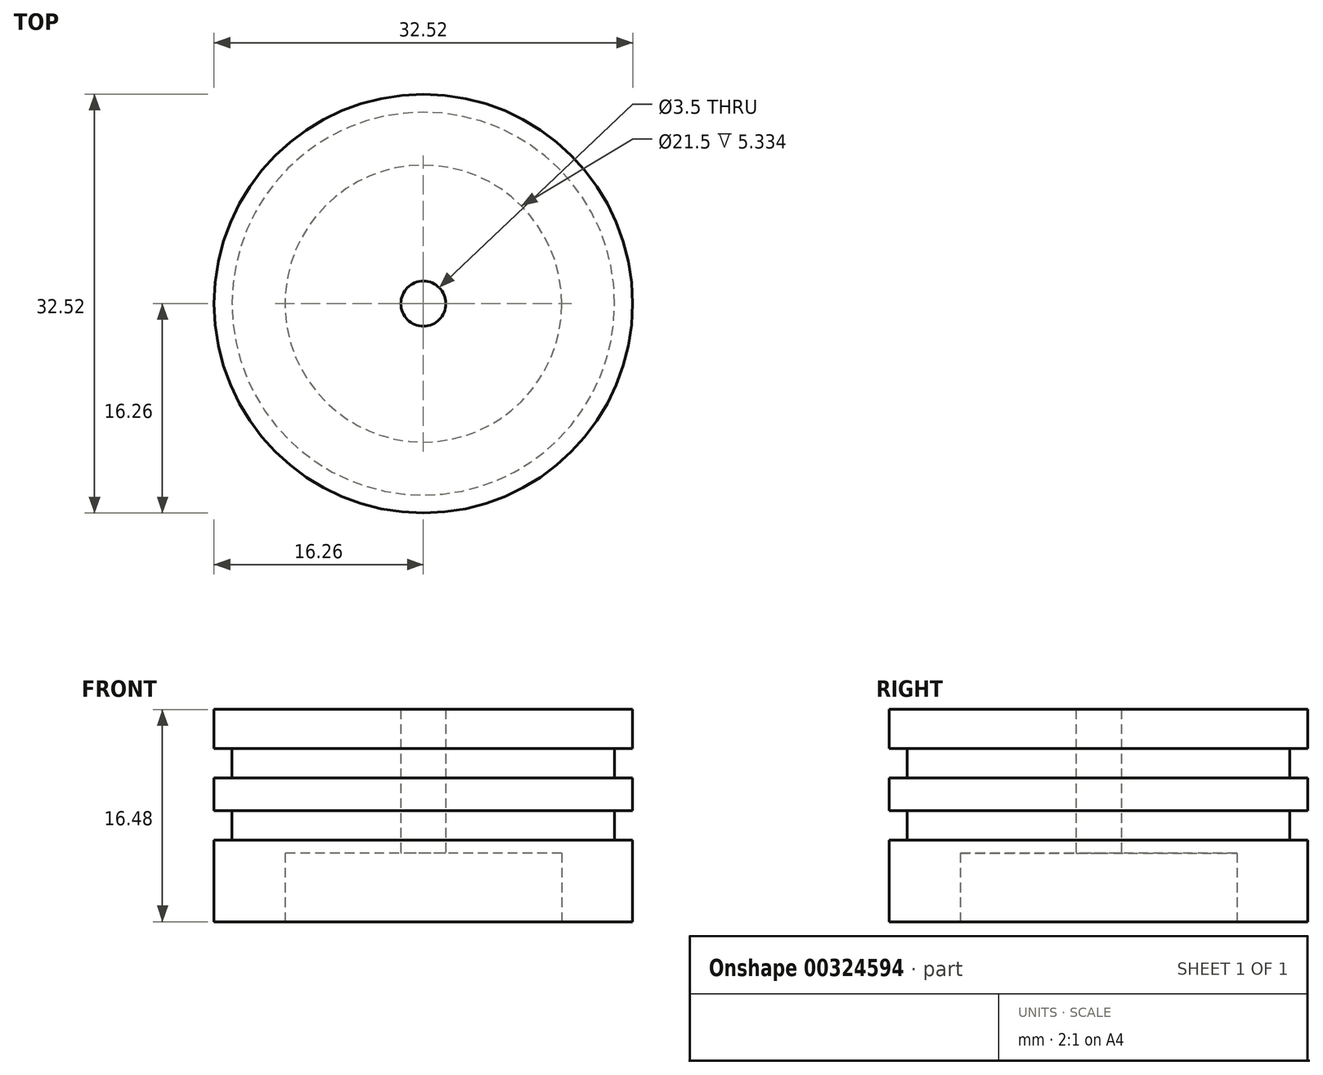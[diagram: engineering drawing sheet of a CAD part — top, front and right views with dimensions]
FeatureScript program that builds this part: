
annotation { "Feature Type Name" : "Feature", "Feature Type Description" : "" }
export const myFeature = defineFeature(function(context is Context, id is Id, definition is map)
    precondition{}
    {
        {
            var Q0;
            Q0=qCreatedBy(makeId("Top.planeOp"),FACE);
            var sketch = newSketch(context, id + "F0", { "sketchPlane" : qUnion([Q0])});
            skCircle(sketch, "E0", {"center": v(0, 0) * mm, "radius": 16.26 * mm});
            skSolve(sketch);
        }
        {
            var Q0;
            Q0 = qSketchRegion(id + "F0", true);
            extrude(context, id + "F1", {"entities" : qUnion([Q0]), "depth" : 6.35 * mm});
        }
        {
            var Q0;
            Q0=qCreatedBy(makeId("Top.planeOp"),FACE);
            var sketch = newSketch(context, id + "F2", { "sketchPlane" : qUnion([Q0])});
            skCircle(sketch, "E1", {"center": v(0, 0) * mm, "radius": 14.86 * mm});
            skSolve(sketch);
        }
        {
            var Q0;
            Q0 = qSketchRegion(id + "F2", true);
            extrude(context, id + "F3", {"entities" : qUnion([Q0]), "operationType" : NewBodyOperationType.ADD, "depth" : 16 * mm});
        }
        {
            var Q0;
            Q0=qCreatedBy(makeId("Top.planeOp"),FACE);
            cPlane(context, id + "F4", {"entities" : qUnion([Q0]), "cplaneType" : CPlaneType.OFFSET, "offset" : 8.64 * mm, "width" : 152.4 * mm, "height" : 152.4 * mm});
        }
        {
            var Q0;
            Q0=qCreatedBy(id+"F4.planeOp",FACE);
            var sketch = newSketch(context, id + "F5", { "sketchPlane" : qUnion([Q0])});
            skCircle(sketch, "E2", {"center": v(0, 0) * mm, "radius": 16.26 * mm});
            skSolve(sketch);
        }
        {
            var Q0;
            Q0 = qSketchRegion(id + "F5", true);
            extrude(context, id + "F6", {"entities" : qUnion([Q0]), "operationType" : NewBodyOperationType.ADD, "depth" : 2.54 * mm});
        }
        {
            var Q0;
            Q0=qCreatedBy(makeId("Top.planeOp"),FACE);
            cPlane(context, id + "F7", {"entities" : qUnion([Q0]), "cplaneType" : CPlaneType.OFFSET, "offset" : 13.46 * mm, "width" : 152.4 * mm, "height" : 152.4 * mm});
        }
        {
            var Q0;
            Q0=qCreatedBy(id+"F7.planeOp",FACE);
            var sketch = newSketch(context, id + "F8", { "sketchPlane" : qUnion([Q0])});
            skCircle(sketch, "E3", {"center": v(0, 0) * mm, "radius": 16.26 * mm});
            skSolve(sketch);
        }
        {
            var Q0;
            Q0 = qSketchRegion(id + "F8", true);
            extrude(context, id + "F9", {"entities" : qUnion([Q0]), "operationType" : NewBodyOperationType.ADD, "depth" : 3.02 * mm});
        }
        {
            var Q0;
            Q0=qCreatedBy(id+"F7.planeOp",FACE);
            var sketch = newSketch(context, id + "F10", { "sketchPlane" : qUnion([Q0])});
            skCircle(sketch, "E4", {"center": v(0, 0) * mm, "radius": 1.75 * mm});
            skSolve(sketch);
        }
        {
            var Q0;
            Q0 = qSketchRegion(id + "F10", true);
            extrude(context, id + "F11", {"entities" : qUnion([Q0]), "operationType" : NewBodyOperationType.REMOVE, "depth" : 42.67 * mm});
        }
        {
            var Q0;
            Q0=qCreatedBy(makeId("Top.planeOp"),FACE);
            var sketch = newSketch(context, id + "F12", { "sketchPlane" : qUnion([Q0])});
            skCircle(sketch, "E5", {"center": v(0, 0) * mm, "radius": 1.75 * mm});
            skSolve(sketch);
        }
        {
            var Q0;
            Q0 = qSketchRegion(id + "F12", true);
            extrude(context, id + "F13", {"entities" : qUnion([Q0]), "operationType" : NewBodyOperationType.REMOVE, "depth" : 37.08 * mm});
        }
        {
            var Q0;
            Q0=qCreatedBy(makeId("Top.planeOp"),FACE);
            var sketch = newSketch(context, id + "F14", { "sketchPlane" : qUnion([Q0])});
            skCircle(sketch, "E6", {"center": v(0, 0) * mm, "radius": 10.75 * mm});
            skSolve(sketch);
        }
        {
            var Q0;
            Q0 = qSketchRegion(id + "F14", true);
            extrude(context, id + "F15", {"entities" : qUnion([Q0]), "operationType" : NewBodyOperationType.REMOVE, "depth" : 5.33 * mm});
        }
    });
